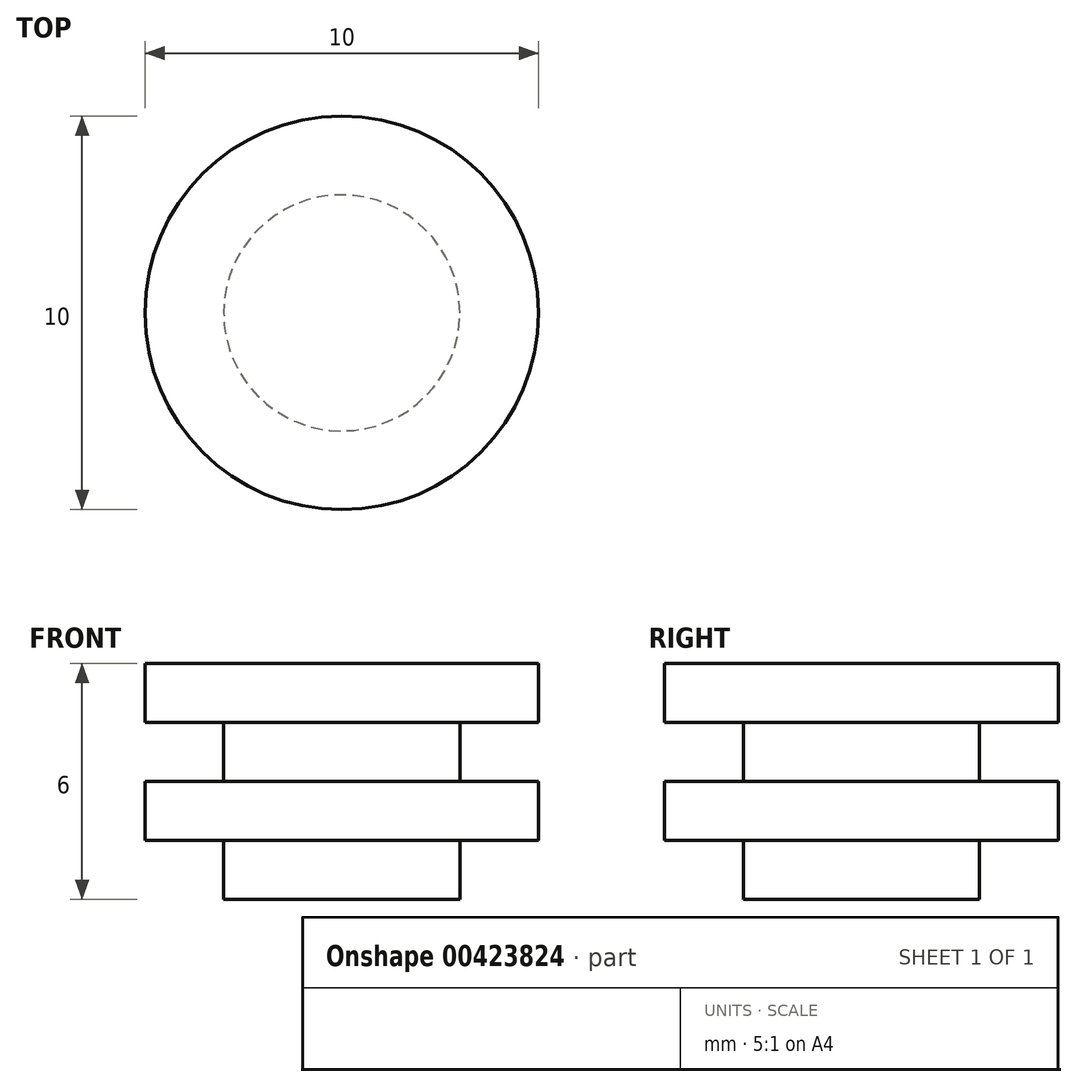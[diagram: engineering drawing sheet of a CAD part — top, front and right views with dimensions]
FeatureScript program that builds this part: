
annotation { "Feature Type Name" : "Feature", "Feature Type Description" : "" }
export const myFeature = defineFeature(function(context is Context, id is Id, definition is map)
    precondition{}
    {
        {
            var Q0;
            Q0=qCreatedBy(makeId("Front.planeOp"),FACE);
            var sketch = newSketch(context, id + "F0", { "sketchPlane" : qUnion([Q0])});
            skLineSegment(sketch, "E0", {"start": v(3, 0) * mm, "end": v(3, 1.5) * mm});
            skLineSegment(sketch, "E1", {"start": v(3, 1.5) * mm, "end": v(5, 1.5) * mm});
            skLineSegment(sketch, "E2", {"start": v(5, 1.5) * mm, "end": v(5, 3) * mm});
            skLineSegment(sketch, "E3", {"start": v(5, 3) * mm, "end": v(3, 3) * mm});
            skLineSegment(sketch, "E4", {"start": v(3, 3) * mm, "end": v(3, 4.5) * mm});
            skLineSegment(sketch, "E5", {"start": v(3, 4.5) * mm, "end": v(5, 4.5) * mm});
            skLineSegment(sketch, "E6", {"start": v(5, 4.5) * mm, "end": v(5, 6) * mm});
            skLineSegment(sketch, "E7", {"start": v(5, 6) * mm, "end": v(0, 6) * mm});
            skLineSegment(sketch, "E8", {"start": v(0, 6) * mm, "end": v(0, 0) * mm});
            skLineSegment(sketch, "E9", {"start": v(0, 0) * mm, "end": v(3, 0) * mm});
            skSolve(sketch);
        }
        {
            var Q0;
            Q0=makeQuery(id+"F0.imprint","IMPRINT",FACE,{"disambiguationData":[TD([[makeQuery(id+"F0.imprint","IMPRINT",EDGE,{"derivedFrom":sQuery(id+"F0.wireOp",EDGE,"E0")}),1.0]])]});
            var Q1;
            Q1=sQuery(id+"F0.wireOp",EDGE,"E8");
            revolve(context, id + "F1", {"entities" : qUnion([Q0]), "axis" : qUnion([Q1]), "revolveType" : RevolveType.FULL});
        }
    });
